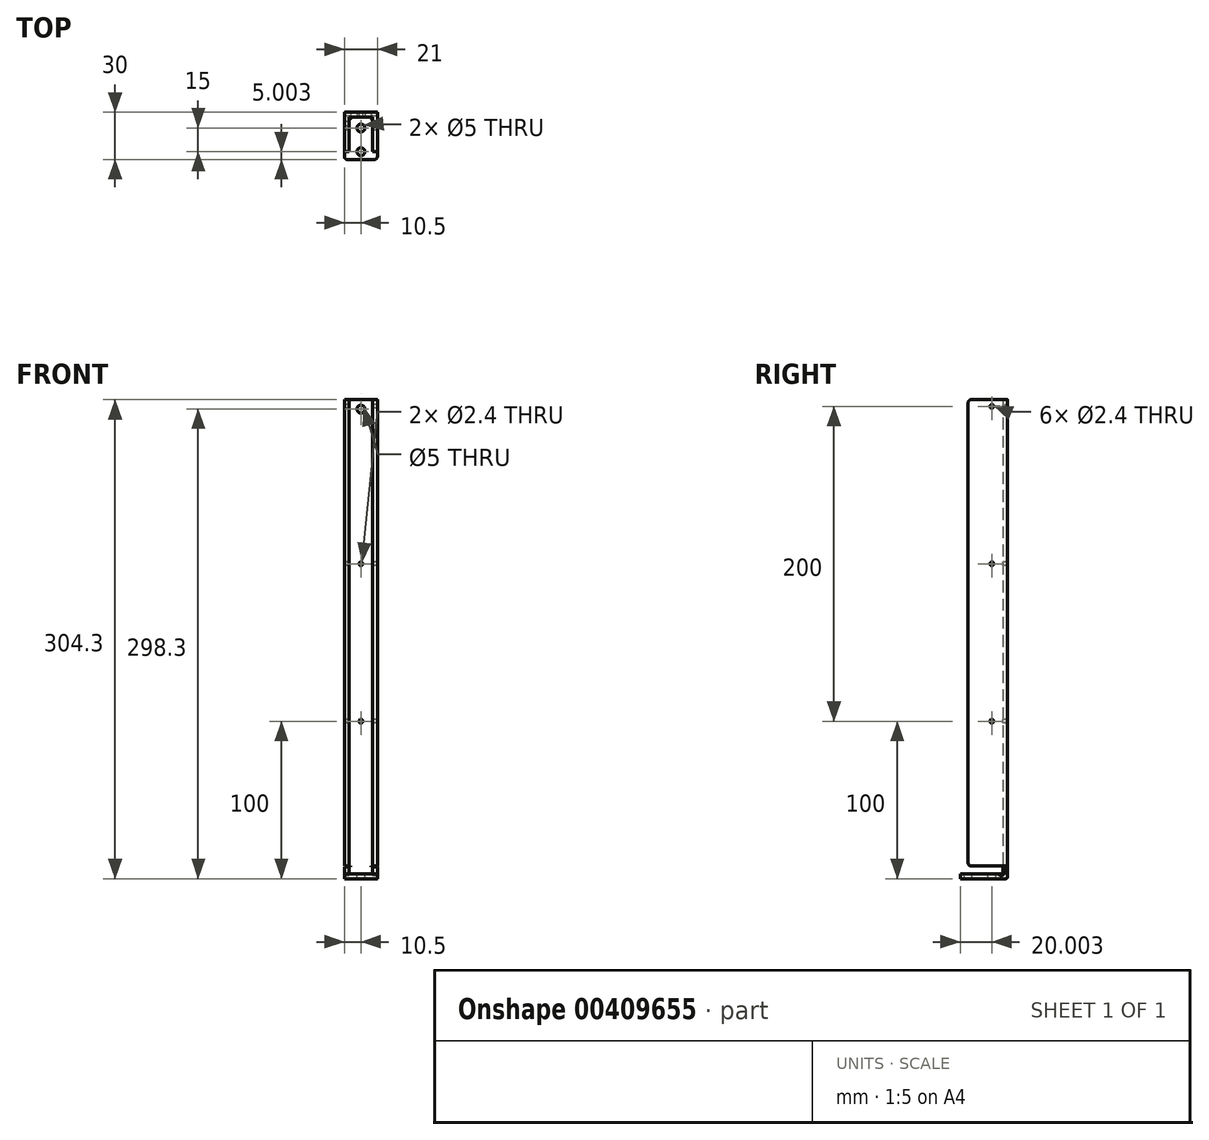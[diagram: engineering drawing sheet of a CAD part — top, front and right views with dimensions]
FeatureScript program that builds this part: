
annotation { "Feature Type Name" : "Feature", "Feature Type Description" : "" }
export const myFeature = defineFeature(function(context is Context, id is Id, definition is map)
    precondition{}
    {
        {
            var Q0;
            Q0=qCreatedBy(makeId("Right.planeOp"),FACE);
            var sketch = newSketch(context, id + "F0", { "sketchPlane" : qUnion([Q0])});
            skLineSegment(sketch, "E0", {"start": v(-7.6, 0) * mm, "end": v(22.4, 0) * mm});
            skLineSegment(sketch, "E1", {"start": v(22.4, 0) * mm, "end": v(22.4, 304.3) * mm});
            skLineSegment(sketch, "E2", {"start": v(22.4, 304.3) * mm, "end": v(19.4, 304.3) * mm});
            skLineSegment(sketch, "E3", {"start": v(19.4, 304.3) * mm, "end": v(19.4, 3) * mm});
            skLineSegment(sketch, "E4", {"start": v(19.4, 3) * mm, "end": v(-7.6, 3) * mm});
            skLineSegment(sketch, "E5", {"start": v(-7.6, 3) * mm, "end": v(-7.6, 0) * mm});
            skSolve(sketch);
        }
        {
            var Q0;
            Q0=qSketchRegion(id+"F0",true);
            extrude(context, id + "F1", {"entities" : qUnion([Q0]), "depth" : 15 * mm});
        }
        {
            var Q0;
            Q0=makeQuery(id+"F1.opExtrude","SWEPT_FACE",FACE,{"disambiguationData":[OSD([sQuery(id+"F0.wireOp",EDGE,"E1")])]});
            var sketch = newSketch(context, id + "F2", { "sketchPlane" : qUnion([Q0])});
            skLineSegment(sketch, "E6.bottom", {"start": v(0, 8) * mm, "end": v(3, 8) * mm});
            skLineSegment(sketch, "E6.top", {"start": v(0, 304.3) * mm, "end": v(3, 304.3) * mm});
            skLineSegment(sketch, "E6.left", {"start": v(0, 8) * mm, "end": v(0, 304.3) * mm});
            skLineSegment(sketch, "E6.right", {"start": v(3, 8) * mm, "end": v(3, 304.3) * mm});
            skLineSegment(sketch, "E7.bottom", {"start": v(-15, 304.3) * mm, "end": v(-18, 304.3) * mm});
            skLineSegment(sketch, "E7.top", {"start": v(-15, 8) * mm, "end": v(-18, 8) * mm});
            skLineSegment(sketch, "E7.left", {"start": v(-15, 304.3) * mm, "end": v(-15, 8) * mm});
            skLineSegment(sketch, "E7.right", {"start": v(-18, 304.3) * mm, "end": v(-18, 8) * mm});
            skSolve(sketch);
        }
        {
            var Q0;
            Q0=qSketchRegion(id+"F2",true);
            extrude(context, id + "F3", {"entities" : qUnion([Q0]), "operationType" : NewBodyOperationType.ADD, "oppositeDirection" : true, "depth" : 25 * mm});
        }
        {
            var Q0;
            Q0=makeQuery(id+"F1.opExtrude","SWEPT_FACE",FACE,{"disambiguationData":[OSD([sQuery(id+"F0.wireOp",EDGE,"E4")])]});
            var sketch = newSketch(context, id + "F4", { "sketchPlane" : qUnion([Q0])});
            skCircle(sketch, "E8", {"center": v(7.5, -2.6) * mm, "radius": 2.5 * mm});
            skCircle(sketch, "E9", {"center": v(7.5, 12.4) * mm, "radius": 2.5 * mm});
            skSolve(sketch);
        }
        {
            var Q0;
            Q0=qSketchRegion(id+"F4",true);
            extrude(context, id + "F5", {"entities" : qUnion([Q0]), "operationType" : NewBodyOperationType.REMOVE, "oppositeDirection" : true, "depth" : 3 * mm});
        }
        {
            var Q0;
            Q0=makeQuery(id+"F1.opExtrude","SWEPT_FACE",FACE,{"disambiguationData":[OSD([sQuery(id+"F0.wireOp",EDGE,"E3")])]});
            var sketch = newSketch(context, id + "F6", { "sketchPlane" : qUnion([Q0])});
            skLineSegment(sketch, "E10.bottom", {"start": v(0, 8) * mm, "end": v(1, 8) * mm});
            skLineSegment(sketch, "E10.top", {"start": v(0, 7.5) * mm, "end": v(1, 7.5) * mm});
            skLineSegment(sketch, "E10.left", {"start": v(0, 8) * mm, "end": v(0, 7.5) * mm});
            skLineSegment(sketch, "E10.right", {"start": v(1, 8) * mm, "end": v(1, 7.5) * mm});
            skLineSegment(sketch, "E11.bottom", {"start": v(15, 8) * mm, "end": v(14, 8) * mm});
            skLineSegment(sketch, "E11.top", {"start": v(15, 7.5) * mm, "end": v(14, 7.5) * mm});
            skLineSegment(sketch, "E11.left", {"start": v(15, 8) * mm, "end": v(15, 7.5) * mm});
            skLineSegment(sketch, "E11.right", {"start": v(14, 8) * mm, "end": v(14, 7.5) * mm});
            skSolve(sketch);
        }
        {
            var Q0;
            Q0=qSketchRegion(id+"F6",true);
            extrude(context, id + "F7", {"entities" : qUnion([Q0]), "operationType" : NewBodyOperationType.REMOVE, "oppositeDirection" : true, "depth" : 3 * mm});
        }
        {
            var Q0;
            Q0=makeQuery(id+"F1.opExtrude","SWEPT_EDGE",EDGE,{"disambiguationData":[OSD([sQuery(id+"F0.wireOp",EDGE,"E3"),sQuery(id+"F0.wireOp",EDGE,"E4")])]});
            var Q1;
            Q1=makeQuery(id+"F1.opExtrude","SWEPT_EDGE",EDGE,{"disambiguationData":[OSD([sQuery(id+"F0.wireOp",EDGE,"E0"),sQuery(id+"F0.wireOp",EDGE,"E1")])]});
            var Q2;
            {var subQ0=sQuery(id+"F0.wireOp",EDGE,"E3");Q2=makeQuery(id+"F3.boolean.opBoolean","SPLIT",EDGE,{"disambiguationData":[topologyDisambiguationEdgeConnected([makeQuery(id+"F3.opExtrude","SWEPT_FACE",FACE,{"disambiguationData":[OSD([sQuery(id+"F2.wireOp",EDGE,"E6.left")])]})])],"derivedFrom":makeQuery(id+"F1.opExtrude","CAP_EDGE",EDGE,{"disambiguationData":[OSD([subQ0])],"isStart":true})});}
            var Q3;
            Q3=makeQuery(id+"F3.opExtrude","CAP_EDGE",EDGE,{"disambiguationData":[OSD([sQuery(id+"F2.wireOp",EDGE,"E6.right")])],"isStart":true});
            var Q4;
            Q4=makeQuery(id+"F3.opExtrude","CAP_EDGE",EDGE,{"disambiguationData":[OSD([sQuery(id+"F2.wireOp",EDGE,"E7.right")])],"isStart":true});
            var Q5;
            {var subQ0=sQuery(id+"F0.wireOp",EDGE,"E3");Q5=makeQuery(id+"F3.boolean.opBoolean","SPLIT",EDGE,{"disambiguationData":[topologyDisambiguationEdgeConnected([makeQuery(id+"F3.opExtrude","SWEPT_FACE",FACE,{"disambiguationData":[OSD([sQuery(id+"F2.wireOp",EDGE,"E7.left")])]})])],"derivedFrom":makeQuery(id+"F1.opExtrude","CAP_EDGE",EDGE,{"disambiguationData":[OSD([subQ0])],"isStart":false})});}
            fillet(context, id + "F8", {"entities" : qUnion([Q0, Q1, Q2, Q3, Q4, Q5]), "radius" : 1 * mm, "tangentPropagation" : true, "allowEdgeOverflow" : false});
        }
        {
            var Q0;
            Q0=makeQuery(id+"F1.opExtrude","SWEPT_FACE",FACE,{"disambiguationData":[OSD([sQuery(id+"F0.wireOp",EDGE,"E3")])]});
            var sketch = newSketch(context, id + "F9", { "sketchPlane" : qUnion([Q0])});
            skCircle(sketch, "E12", {"center": v(7.5, 298.3) * mm, "radius": 2.5 * mm});
            skPoint(sketch, "E12.centerSnap0", {"position": v(7.5, 304.3) * mm});
            skCircle(sketch, "E13", {"center": v(7.5, 100) * mm, "radius": 1.2 * mm});
            skPoint(sketch, "E13.centerSnap0", {"position": v(7.5, 4) * mm});
            skCircle(sketch, "E14", {"center": v(7.5, 200) * mm, "radius": 1.2 * mm});
            skSolve(sketch);
        }
        {
            var Q0;
            Q0=qSketchRegion(id+"F9",true);
            extrude(context, id + "F10", {"entities" : qUnion([Q0]), "operationType" : NewBodyOperationType.REMOVE, "oppositeDirection" : true, "depth" : 3 * mm});
        }
        {
            var Q0;
            Q0=makeQuery(id+"F3.opExtrude","SWEPT_FACE",FACE,{"disambiguationData":[OSD([sQuery(id+"F2.wireOp",EDGE,"E6.right")])]});
            var sketch = newSketch(context, id + "F11", { "sketchPlane" : qUnion([Q0])});
            skCircle(sketch, "E15", {"center": v(-12.4, 200) * mm, "radius": 1.2 * mm});
            skCircle(sketch, "E16", {"center": v(-12.4, 100) * mm, "radius": 1.2 * mm});
            skCircle(sketch, "E17", {"center": v(-12.4, 300) * mm, "radius": 1.2 * mm});
            skSolve(sketch);
        }
        {
            var Q0;
            Q0=qSketchRegion(id+"F11",true);
            extrude(context, id + "F12", {"entities" : qUnion([Q0]), "operationType" : NewBodyOperationType.REMOVE, "oppositeDirection" : true, "depth" : 34.2 * mm});
        }
        {
            var Q0;
            Q0=makeQuery(id+"F1.opExtrude","CAP_FACE",FACE,{"disambiguationData":[OSD([sQuery(id+"F0.wireOp",EDGE,"E0"),sQuery(id+"F0.wireOp",EDGE,"E1"),sQuery(id+"F0.wireOp",EDGE,"E2"),sQuery(id+"F0.wireOp",EDGE,"E3"),sQuery(id+"F0.wireOp",EDGE,"E4"),sQuery(id+"F0.wireOp",EDGE,"E5")])],"isStart":true});
            var Q1;
            Q1=makeQuery(id+"F1.opExtrude","CAP_FACE",FACE,{"disambiguationData":[OSD([sQuery(id+"F0.wireOp",EDGE,"E0"),sQuery(id+"F0.wireOp",EDGE,"E1"),sQuery(id+"F0.wireOp",EDGE,"E2"),sQuery(id+"F0.wireOp",EDGE,"E3"),sQuery(id+"F0.wireOp",EDGE,"E4"),sQuery(id+"F0.wireOp",EDGE,"E5")])],"isStart":false});
            extrude(context, id + "F13", {"entities" : qUnion([Q0, Q1]), "operationType" : NewBodyOperationType.ADD, "endBound" : BoundingType.SYMMETRIC, "depth" : 6 * mm});
        }
        {
            var Q0;
            {var subQ0=sQuery(id+"F0.wireOp",EDGE,"E5");Q0=makeQuery(id+"F13.opExtrude","CAP_EDGE",EDGE,{"disambiguationData":[OSD([subQ0]),TDD([makeQuery(id+"F1.opExtrude","CAP_EDGE",EDGE,{"disambiguationData":[OSD([subQ0])],"isStart":true})])],"isStart":false});}
            var Q1;
            {var subQ0=sQuery(id+"F0.wireOp",EDGE,"E5");Q1=makeQuery(id+"F13.opExtrude","CAP_EDGE",EDGE,{"disambiguationData":[OSD([subQ0]),TDD([makeQuery(id+"F1.opExtrude","CAP_EDGE",EDGE,{"disambiguationData":[OSD([subQ0])],"isStart":false})])],"isStart":true});}
            var Q2;
            Q2=makeQuery(id+"F3.opExtrude","CAP_EDGE",EDGE,{"disambiguationData":[OSD([sQuery(id+"F2.wireOp",EDGE,"E7.top")])],"isStart":false});
            var Q3;
            Q3=makeQuery(id+"F3.opExtrude","CAP_EDGE",EDGE,{"disambiguationData":[OSD([sQuery(id+"F2.wireOp",EDGE,"E6.bottom")])],"isStart":false});
            var Q4;
            Q4=makeQuery(id+"F3.opExtrude","CAP_EDGE",EDGE,{"disambiguationData":[OSD([sQuery(id+"F2.wireOp",EDGE,"E6.top")])],"isStart":false});
            var Q5;
            Q5=makeQuery(id+"F3.opExtrude","CAP_EDGE",EDGE,{"disambiguationData":[OSD([sQuery(id+"F2.wireOp",EDGE,"E7.bottom")])],"isStart":false});
            fillet(context, id + "F14", {"entities" : qUnion([Q0, Q1, Q2, Q3, Q4, Q5]), "radius" : 2 * mm, "tangentPropagation" : true, "allowEdgeOverflow" : false});
        }
    });
